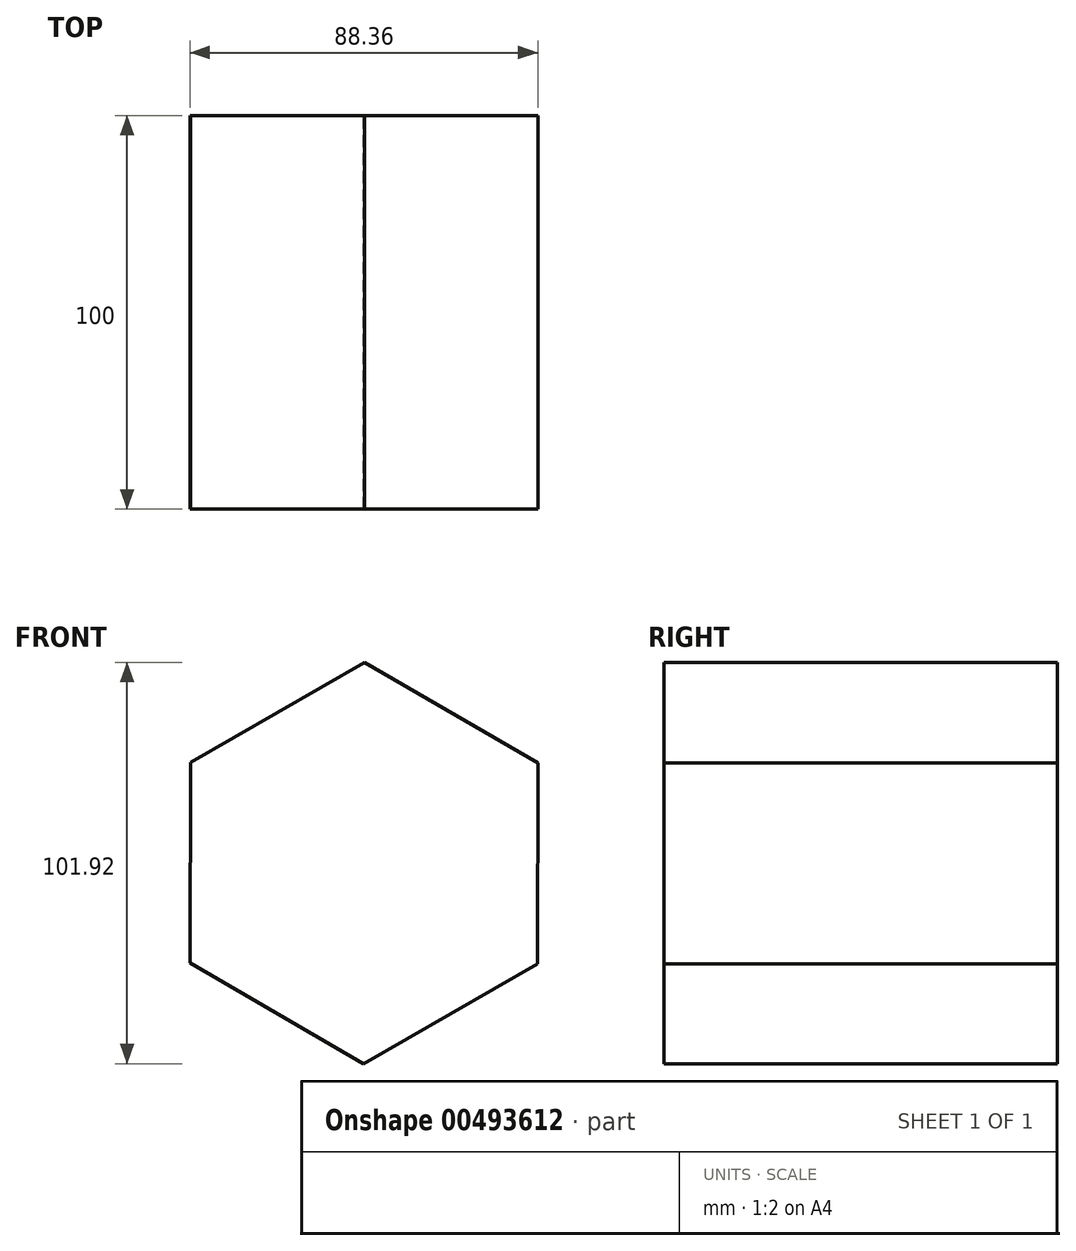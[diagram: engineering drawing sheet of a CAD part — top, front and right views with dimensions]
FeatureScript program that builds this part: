
annotation { "Feature Type Name" : "Feature", "Feature Type Description" : "" }
export const myFeature = defineFeature(function(context is Context, id is Id, definition is map)
    precondition{}
    {
        {
            var Q0;
            Q0=qCreatedBy(makeId("Front.planeOp"),FACE);
            var sketch = newSketch(context, id + "F0", { "sketchPlane" : qUnion([Q0])});
            skCircle(sketch, "E0.cCircle", {"center": v(0, 0) * mm, "radius": 50.96 * mm, "construction": true});
            skLineSegment(sketch, "E0.0", {"start": v(-44.18, -25.39) * mm, "end": v(-44.08, 25.57) * mm});
            skLineSegment(sketch, "E0.1", {"start": v(-44.08, 25.57) * mm, "end": v(0.1, 50.96) * mm});
            skLineSegment(sketch, "E0.2", {"start": v(0.1, 50.96) * mm, "end": v(44.18, 25.39) * mm});
            skLineSegment(sketch, "E0.3", {"start": v(44.18, 25.39) * mm, "end": v(44.08, -25.57) * mm});
            skLineSegment(sketch, "E0.4", {"start": v(44.08, -25.57) * mm, "end": v(-0.1, -50.96) * mm});
            skLineSegment(sketch, "E0.5", {"start": v(-0.1, -50.96) * mm, "end": v(-44.18, -25.39) * mm});
            skSolve(sketch);
        }
        {
            var Q0;
            Q0=makeQuery(id+"F0.imprint","IMPRINT",FACE,{"disambiguationData":[TD([[makeQuery(id+"F0.imprint","IMPRINT",EDGE,{"derivedFrom":sQuery(id+"F0.wireOp",EDGE,"E0.0")}),-1.0]])]});
            extrude(context, id + "F1", {"entities" : qUnion([Q0]), "depth" : 100 * mm});
        }
    });
